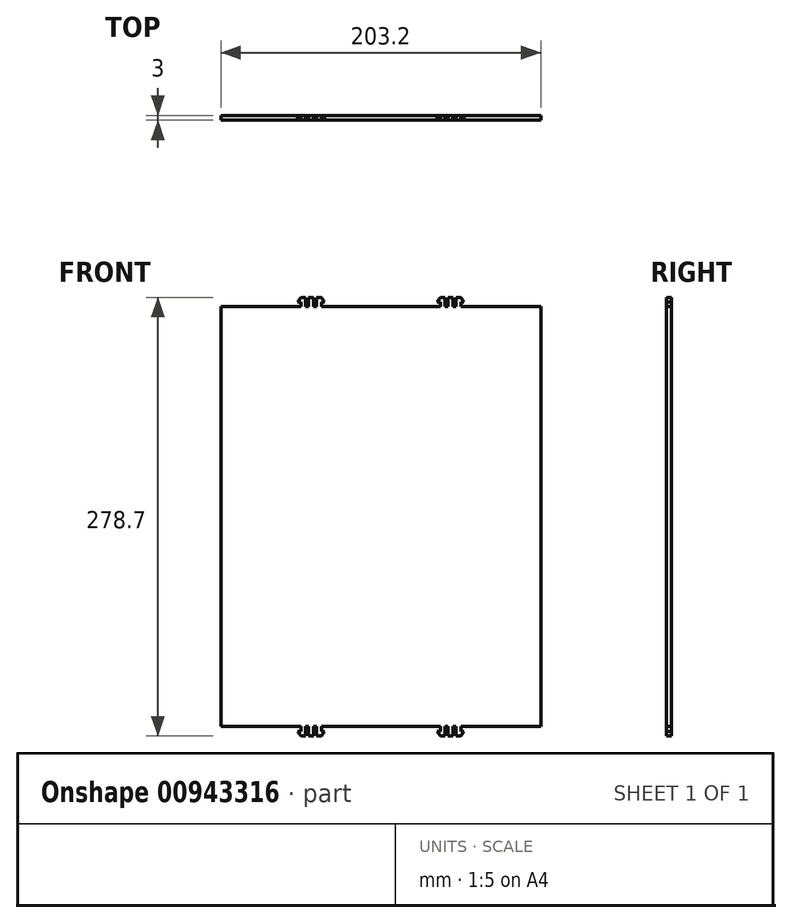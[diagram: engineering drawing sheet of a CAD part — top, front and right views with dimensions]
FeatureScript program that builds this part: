
annotation { "Feature Type Name" : "Feature", "Feature Type Description" : "" }
export const myFeature = defineFeature(function(context is Context, id is Id, definition is map)
    precondition{}
    {
        {
            var Q0;
            Q0=qCreatedBy(makeId("Front.planeOp"),FACE);
            var sketch = newSketch(context, id + "F0", { "sketchPlane" : qUnion([Q0])});
            skLineSegment(sketch, "E0.left", {"start": v(111.81, 180) * mm, "end": v(111.81, -86.7) * mm});
            skLineSegment(sketch, "E0.right", {"start": v(-91.39, 180) * mm, "end": v(-91.39, -86.7) * mm});
            skPoint(sketch, "E0.middle", {"position": v(10.21, 46.66) * mm});
            skLineSegment(sketch, "E1", {"start": v(-40.59, 180) * mm, "end": v(-40.59, 183) * mm});
            skLineSegment(sketch, "E2", {"start": v(-42.59, 183) * mm, "end": v(-40.59, 186) * mm});
            skLineSegment(sketch, "E3", {"start": v(-40.59, 186) * mm, "end": v(-37.59, 186) * mm});
            skLineSegment(sketch, "E4", {"start": v(-37.59, 186) * mm, "end": v(-37.59, 180) * mm});
            skLineSegment(sketch, "E5", {"start": v(-37.59, 180) * mm, "end": v(-35.59, 180) * mm});
            skLineSegment(sketch, "E6", {"start": v(-35.59, 180) * mm, "end": v(-35.59, 186) * mm});
            skLineSegment(sketch, "E7", {"start": v(-35.59, 186) * mm, "end": v(-32.59, 186) * mm});
            skLineSegment(sketch, "E8", {"start": v(-32.59, 186) * mm, "end": v(-32.59, 180) * mm});
            skLineSegment(sketch, "E9", {"start": v(-32.59, 180) * mm, "end": v(-30.59, 180) * mm});
            skLineSegment(sketch, "E10", {"start": v(-30.59, 180) * mm, "end": v(-30.59, 186) * mm});
            skLineSegment(sketch, "E11", {"start": v(-30.59, 186) * mm, "end": v(-27.59, 186) * mm});
            skLineSegment(sketch, "E12", {"start": v(-27.59, 186) * mm, "end": v(-25.59, 183) * mm});
            skLineSegment(sketch, "E13", {"start": v(-25.59, 183) * mm, "end": v(-27.59, 183) * mm});
            skLineSegment(sketch, "E14", {"start": v(-27.59, 183) * mm, "end": v(-27.59, 180) * mm});
            skLineSegment(sketch, "E15", {"start": v(-42.59, 183) * mm, "end": v(-40.59, 183) * mm});
            skLineSegment(sketch, "E16.trimOffspring", {"start": v(-40.59, 180) * mm, "end": v(-91.39, 180) * mm});
            skLineSegment(sketch, "E17", {"start": v(-27.59, 180) * mm, "end": v(111.81, 180) * mm});
            skLineSegment(sketch, "E18", {"start": v(48.01, 180) * mm, "end": v(48.01, 183) * mm});
            skLineSegment(sketch, "E19", {"start": v(46.01, 183) * mm, "end": v(48.02, 186) * mm});
            skLineSegment(sketch, "E20", {"start": v(48.02, 186) * mm, "end": v(51.01, 186) * mm});
            skLineSegment(sketch, "E21", {"start": v(51.01, 186) * mm, "end": v(51.01, 180) * mm});
            skLineSegment(sketch, "E22", {"start": v(51.01, 180) * mm, "end": v(53.01, 180) * mm});
            skLineSegment(sketch, "E23", {"start": v(53.01, 180) * mm, "end": v(53.01, 186) * mm});
            skLineSegment(sketch, "E24", {"start": v(53.01, 186) * mm, "end": v(56.01, 186) * mm});
            skLineSegment(sketch, "E25", {"start": v(56.01, 186) * mm, "end": v(56.01, 180) * mm});
            skLineSegment(sketch, "E26", {"start": v(56.01, 180) * mm, "end": v(58.01, 180) * mm});
            skLineSegment(sketch, "E27", {"start": v(58.01, 180) * mm, "end": v(58.01, 186) * mm});
            skLineSegment(sketch, "E28", {"start": v(58.01, 186) * mm, "end": v(61.01, 186) * mm});
            skLineSegment(sketch, "E29", {"start": v(61.01, 186) * mm, "end": v(63.01, 183) * mm});
            skLineSegment(sketch, "E30", {"start": v(63.01, 183) * mm, "end": v(61.01, 183) * mm});
            skLineSegment(sketch, "E31", {"start": v(61.01, 183) * mm, "end": v(61.01, 180) * mm});
            skLineSegment(sketch, "E32", {"start": v(46.01, 183) * mm, "end": v(48.01, 183) * mm});
            skLineSegment(sketch, "E33.MirrorCS", {"start": v(-27.59, -89.7) * mm, "end": v(-27.59, -86.7) * mm});
            skLineSegment(sketch, "E34.MirrorCS", {"start": v(-25.59, -89.7) * mm, "end": v(-27.59, -89.7) * mm});
            skLineSegment(sketch, "E35.MirrorCS", {"start": v(-27.59, -92.7) * mm, "end": v(-25.59, -89.7) * mm});
            skLineSegment(sketch, "E36.MirrorCS", {"start": v(-42.59, -89.7) * mm, "end": v(-40.59, -89.7) * mm});
            skLineSegment(sketch, "E37.MirrorCS", {"start": v(-40.59, -86.7) * mm, "end": v(-40.59, -89.7) * mm});
            skLineSegment(sketch, "E38.MirrorCS", {"start": v(-42.59, -89.7) * mm, "end": v(-40.59, -92.7) * mm});
            skLineSegment(sketch, "E39.MirrorCS", {"start": v(-40.59, -92.7) * mm, "end": v(-37.59, -92.7) * mm});
            skLineSegment(sketch, "E40.MirrorCS", {"start": v(-32.59, -92.7) * mm, "end": v(-32.59, -86.7) * mm});
            skLineSegment(sketch, "E41.MirrorCS", {"start": v(-30.59, -86.7) * mm, "end": v(-30.59, -92.7) * mm});
            skLineSegment(sketch, "E42.MirrorCS", {"start": v(-37.59, -92.7) * mm, "end": v(-37.59, -86.7) * mm});
            skLineSegment(sketch, "E43.MirrorCS", {"start": v(-35.59, -86.7) * mm, "end": v(-35.59, -92.7) * mm});
            skLineSegment(sketch, "E44.MirrorCS", {"start": v(-30.59, -92.7) * mm, "end": v(-27.59, -92.7) * mm});
            skLineSegment(sketch, "E45.MirrorCS", {"start": v(-35.59, -92.7) * mm, "end": v(-32.59, -92.7) * mm});
            skLineSegment(sketch, "E46", {"start": v(-37.59, -86.7) * mm, "end": v(-35.59, -86.7) * mm});
            skLineSegment(sketch, "E47", {"start": v(-32.59, -86.7) * mm, "end": v(-30.59, -86.7) * mm});
            skLineSegment(sketch, "E48.trimOffspring", {"start": v(-40.59, -86.7) * mm, "end": v(-91.39, -86.7) * mm});
            skLineSegment(sketch, "E49.trimOffspring", {"start": v(-35.59, -86.7) * mm, "end": v(-37.59, -86.7) * mm});
            skLineSegment(sketch, "E50.trimOffspring", {"start": v(-30.59, -86.7) * mm, "end": v(-32.59, -86.7) * mm});
            skLineSegment(sketch, "E51", {"start": v(-27.59, -86.7) * mm, "end": v(48.01, -86.7) * mm});
            skLineSegment(sketch, "E52", {"start": v(111.81, -86.7) * mm, "end": v(61.01, -86.7) * mm});
            skLineSegment(sketch, "E53.MirrorCS", {"start": v(61.01, -89.7) * mm, "end": v(61.01, -86.7) * mm});
            skLineSegment(sketch, "E54.MirrorCS", {"start": v(63.01, -89.7) * mm, "end": v(61.01, -89.7) * mm});
            skLineSegment(sketch, "E55.MirrorCS", {"start": v(61.01, -92.7) * mm, "end": v(63.01, -89.7) * mm});
            skLineSegment(sketch, "E56.MirrorCS", {"start": v(46.01, -89.7) * mm, "end": v(48.01, -89.7) * mm});
            skLineSegment(sketch, "E57.MirrorCS", {"start": v(48.01, -86.7) * mm, "end": v(48.01, -89.7) * mm});
            skLineSegment(sketch, "E58.MirrorCS", {"start": v(46.01, -89.7) * mm, "end": v(48.01, -92.7) * mm});
            skLineSegment(sketch, "E59.MirrorCS", {"start": v(48.01, -92.7) * mm, "end": v(51.01, -92.7) * mm});
            skLineSegment(sketch, "E60.MirrorCS", {"start": v(56.01, -92.7) * mm, "end": v(56.01, -86.7) * mm});
            skLineSegment(sketch, "E61.MirrorCS", {"start": v(58.01, -86.7) * mm, "end": v(58.01, -92.7) * mm});
            skLineSegment(sketch, "E62.MirrorCS", {"start": v(51.01, -92.7) * mm, "end": v(51.01, -86.7) * mm});
            skLineSegment(sketch, "E63.MirrorCS", {"start": v(53.01, -86.7) * mm, "end": v(53.01, -92.7) * mm});
            skLineSegment(sketch, "E64.MirrorCS", {"start": v(58.01, -92.7) * mm, "end": v(61.01, -92.7) * mm});
            skLineSegment(sketch, "E65.MirrorCS", {"start": v(53.01, -92.7) * mm, "end": v(56.01, -92.7) * mm});
            skLineSegment(sketch, "E66", {"start": v(51.01, -86.7) * mm, "end": v(53.01, -86.7) * mm});
            skLineSegment(sketch, "E67", {"start": v(56.01, -86.7) * mm, "end": v(58.01, -86.7) * mm});
            skLineSegment(sketch, "E68.trimOffspring", {"start": v(61.01, -86.7) * mm, "end": v(111.81, -86.7) * mm});
            skSolve(sketch);
        }
        {
            var Q0;
            Q0 = qSketchRegion(id + "F0", true);
            extrude(context, id + "F1", {"entities" : qUnion([Q0]), "depth" : 3 * mm, "offsetDistance" : 25.4 * mm});
        }
    });
